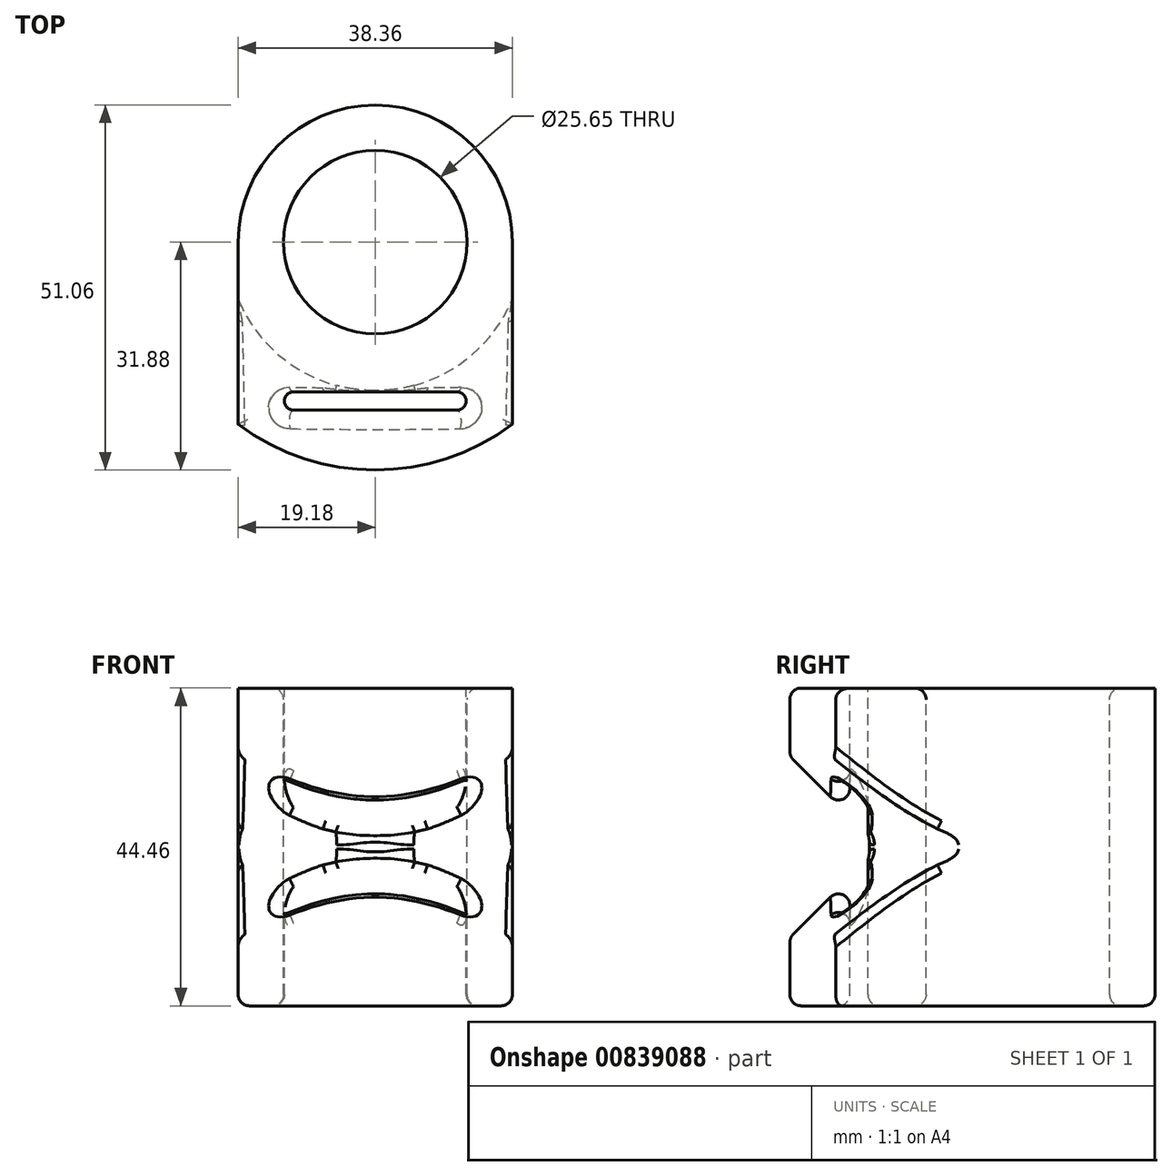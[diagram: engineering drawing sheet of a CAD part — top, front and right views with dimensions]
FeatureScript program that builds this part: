
annotation { "Feature Type Name" : "Feature", "Feature Type Description" : "" }
export const myFeature = defineFeature(function(context is Context, id is Id, definition is map)
    precondition{}
    {
        {
            var Q0;
            Q0=qCreatedBy(makeId("Front.planeOp"),FACE);
            var sketch = newSketch(context, id + "F0", { "sketchPlane" : qUnion([Q0])});
            skLineSegment(sketch, "E0", {"start": v(-12.83, -22.23) * mm, "end": v(-31.88, -22.23) * mm});
            skLineSegment(sketch, "E1", {"start": v(-31.88, -22.23) * mm, "end": v(-31.88, -12.7) * mm});
            skLineSegment(sketch, "E2", {"start": v(-31.88, -12.7) * mm, "end": v(-20.76, -1.59) * mm});
            skLineSegment(sketch, "E3", {"start": v(-20.76, -1.59) * mm, "end": v(-20.76, 0) * mm});
            skLineSegment(sketch, "E4", {"start": v(-12.83, -22.23) * mm, "end": v(-12.83, 0) * mm});
            skLineSegment(sketch, "E5", {"start": v(0, 0) * mm, "end": v(0, -22.22) * mm, "construction": true});
            skLineSegment(sketch, "E6", {"start": v(0, 0) * mm, "end": v(9.66, 0) * mm, "construction": true});
            skLineSegment(sketch, "E7.MirrorCS", {"start": v(-12.83, 22.23) * mm, "end": v(-12.83, 0) * mm});
            skLineSegment(sketch, "E8.MirrorCS", {"start": v(-12.83, 22.23) * mm, "end": v(-31.88, 22.23) * mm});
            skLineSegment(sketch, "E9.MirrorCS", {"start": v(-31.88, 22.23) * mm, "end": v(-31.88, 12.7) * mm});
            skLineSegment(sketch, "E10.MirrorCS", {"start": v(-31.88, 12.7) * mm, "end": v(-20.76, 1.59) * mm});
            skLineSegment(sketch, "E11.MirrorCS", {"start": v(-20.76, 1.59) * mm, "end": v(-20.76, 0) * mm});
            skSolve(sketch);
        }
        {
            var Q0;
            Q0=makeQuery(id+"F0.imprint","IMPRINT",FACE,{"disambiguationData":[TD([[makeQuery(id+"F0.imprint","IMPRINT",EDGE,{"derivedFrom":sQuery(id+"F0.wireOp",EDGE,"E0")}),-1.0]])]});
            var Q1;
            Q1=sQuery(id+"F0.wireOp",EDGE,"E5");
            revolve(context, id + "F1", {"surfaceOperationType" : NewSurfaceOperationType.NEW, "entities" : qUnion([Q0]), "axis" : qUnion([Q1]), "revolveType" : RevolveType.FULL});
        }
        {
            var Q0;
            Q0=makeQuery(id+"F1.opRevolve","SWEPT_FACE",FACE,{"disambiguationData":[OSD([sQuery(id+"F0.wireOp",EDGE,"E8.MirrorCS")])]});
            var sketch = newSketch(context, id + "F2", { "sketchPlane" : qUnion([Q0])});
            skLineSegment(sketch, "E12.bottom", {"start": v(-11.43, -23.5) * mm, "end": v(11.43, -23.5) * mm});
            skLineSegment(sketch, "E12.top", {"start": v(-11.43, -20.96) * mm, "end": v(11.43, -20.96) * mm});
            skLineSegment(sketch, "E12.left", {"start": v(-12.7, -22.23) * mm, "end": v(-12.7, -22.23) * mm});
            skLineSegment(sketch, "E12.right", {"start": v(12.7, -22.23) * mm, "end": v(12.7, -22.23) * mm});
            skPoint(sketch, "E12.middle", {"position": v(0, -22.23) * mm});
            skCircle(sketch, "E13", {"center": v(0, 0) * mm, "radius": 19.18 * mm});
            skLineSegment(sketch, "E14", {"start": v(0, 0) * mm, "end": v(0, -12.83) * mm, "construction": true});
            skLineSegment(sketch, "E15", {"start": v(-19.18, 0) * mm, "end": v(-19.18, -25.46) * mm});
            skLineSegment(sketch, "E16.MirrorCS", {"start": v(19.18, 0) * mm, "end": v(19.18, -25.46) * mm});
            skPoint(sketch, "E17.visualSharp", {"position": v(-12.7, -20.96) * mm});
            skArc(sketch, "E17.filletArc", {"start": v(-11.43, -20.96) * mm, "mid": v(-12.33, -21.33) * mm, "end": v(-12.7, -22.23) * mm});
            skPoint(sketch, "E18.visualSharp", {"position": v(-12.7, -23.5) * mm});
            skArc(sketch, "E18.filletArc", {"start": v(-12.7, -22.23) * mm, "mid": v(-12.33, -23.12) * mm, "end": v(-11.43, -23.5) * mm});
            skPoint(sketch, "E19.visualSharp", {"position": v(12.7, -20.96) * mm});
            skArc(sketch, "E19.filletArc", {"start": v(12.7, -22.23) * mm, "mid": v(12.33, -21.33) * mm, "end": v(11.43, -20.96) * mm});
            skPoint(sketch, "E20.visualSharp", {"position": v(12.7, -23.5) * mm});
            skArc(sketch, "E20.filletArc", {"start": v(11.43, -23.5) * mm, "mid": v(12.33, -23.12) * mm, "end": v(12.7, -22.23) * mm});
            skSolve(sketch);
        }
        {
            var Q0;
            Q0=makeQuery(id+"F2.imprint","IMPRINT",FACE,{"disambiguationData":[TD([[makeQuery(id+"F2.imprint","IMPRINT",EDGE,{"derivedFrom":sQuery(id+"F2.wireOp",EDGE,"E12.bottom")}),1.0]])]});
            extrude(context, id + "F3", {"entities" : qUnion([Q0]), "operationType" : NewBodyOperationType.REMOVE, "endBound" : BoundingType.THROUGH_ALL, "oppositeDirection" : true, "depth" : 25.4 * mm, "offsetDistance" : 25.4 * mm});
        }
        {
            var Q0;
            Q0=makeQuery(id+"F1.opRevolve","SWEPT_EDGE",EDGE,{"disambiguationData":[OSD([sQuery(id+"F0.wireOp",EDGE,"E2"),sQuery(id+"F0.wireOp",EDGE,"E3")])]});
            var Q1;
            Q1=makeQuery(id+"F1.opRevolve","SWEPT_EDGE",EDGE,{"disambiguationData":[OSD([sQuery(id+"F0.wireOp",EDGE,"E10.MirrorCS"),sQuery(id+"F0.wireOp",EDGE,"E11.MirrorCS")])]});
            fillet(context, id + "F4", {"entities" : qUnion([Q0, Q1]), "radius" : 3.17 * mm, "tangentPropagation" : true, "allowEdgeOverflow" : false});
        }
        {
            var Q0;
            {var subQ0=sQuery(id+"F2.wireOp",EDGE,"E15");Q0=makeQuery(id+"F2.imprint","IMPRINT",FACE,{"disambiguationData":[TD([[makeQuery(id+"F2.imprint","IMPRINT",EDGE,{"derivedFrom":subQ0}),-1.0]])]});}
            extrude(context, id + "F5", {"entities" : qUnion([Q0]), "operationType" : NewBodyOperationType.REMOVE, "endBound" : BoundingType.THROUGH_ALL, "oppositeDirection" : true, "depth" : 25.4 * mm, "offsetDistance" : 25.4 * mm});
        }
        {
            var Q0;
            Q0=makeQuery(id+"F1.opRevolve","SWEPT_FACE",FACE,{"disambiguationData":[OSD([sQuery(id+"F0.wireOp",EDGE,"E4"),sQuery(id+"F0.wireOp",EDGE,"E7.MirrorCS")])]});
            var Q1;
            Q1=makeQuery(id+"F5.boolean.opBoolean","COPY",EDGE,{"derivedFrom":makeQuery(id+"F5.opExtrude","CAP_EDGE",EDGE,{"disambiguationData":[OSD([sQuery(id+"F2.wireOp",EDGE,"E15")])],"isStart":true})});
            var Q2;
            Q2=makeQuery(id+"F1.opRevolve","SWEPT_EDGE",EDGE,{"disambiguationData":[OSD([sQuery(id+"F0.wireOp",EDGE,"E8.MirrorCS"),sQuery(id+"F0.wireOp",EDGE,"E9.MirrorCS")])]});
            var Q3;
            Q3=makeQuery(id+"F1.opRevolve","SWEPT_EDGE",EDGE,{"disambiguationData":[OSD([sQuery(id+"F0.wireOp",EDGE,"E0"),sQuery(id+"F0.wireOp",EDGE,"E1")])]});
            var Q4;
            Q4=makeQuery(id+"F5.boolean.opBoolean","INTERSECT",EDGE,{"derivedFrom":[makeQuery(id+"F1.opRevolve","SWEPT_FACE",FACE,{"disambiguationData":[OSD([sQuery(id+"F0.wireOp",EDGE,"E0")])]}),makeQuery(id+"F5.opExtrude","SWEPT_FACE",FACE,{"disambiguationData":[OSD([sQuery(id+"F2.wireOp",EDGE,"E15")])]})]});
            var Q5;
            Q5=makeQuery(id+"F1.opRevolve","SWEPT_EDGE",EDGE,{"disambiguationData":[OSD([sQuery(id+"F0.wireOp",EDGE,"E9.MirrorCS"),sQuery(id+"F0.wireOp",EDGE,"E10.MirrorCS")])]});
            var Q6;
            Q6=makeQuery(id+"F1.opRevolve","SWEPT_EDGE",EDGE,{"disambiguationData":[OSD([sQuery(id+"F0.wireOp",EDGE,"E1"),sQuery(id+"F0.wireOp",EDGE,"E2")])]});
            var Q7;
            Q7=makeQuery(id+"F5.boolean.opBoolean","INTERSECT",EDGE,{"derivedFrom":[makeQuery(id+"F1.opRevolve","SWEPT_FACE",FACE,{"disambiguationData":[OSD([sQuery(id+"F0.wireOp",EDGE,"E2")])]}),makeQuery(id+"F5.opExtrude","SWEPT_FACE",FACE,{"disambiguationData":[OSD([sQuery(id+"F2.wireOp",EDGE,"E15")])]})]});
            var Q8;
            Q8=makeQuery(id+"F5.boolean.opBoolean","INTERSECT",EDGE,{"derivedFrom":[makeQuery(id+"F1.opRevolve","SWEPT_FACE",FACE,{"disambiguationData":[OSD([sQuery(id+"F0.wireOp",EDGE,"E10.MirrorCS")])]}),makeQuery(id+"F5.opExtrude","SWEPT_FACE",FACE,{"disambiguationData":[OSD([sQuery(id+"F2.wireOp",EDGE,"E16.MirrorCS")])]})]});
            var Q9;
            Q9=makeQuery(id+"F5.boolean.opBoolean","INTERSECT",EDGE,{"derivedFrom":[makeQuery(id+"F1.opRevolve","SWEPT_FACE",FACE,{"disambiguationData":[OSD([sQuery(id+"F0.wireOp",EDGE,"E2")])]}),makeQuery(id+"F5.opExtrude","SWEPT_FACE",FACE,{"disambiguationData":[OSD([sQuery(id+"F2.wireOp",EDGE,"E16.MirrorCS")])]})]});
            var Q10;
            Q10=makeQuery(id+"F5.boolean.opBoolean","INTERSECT",EDGE,{"derivedFrom":[makeQuery(id+"F1.opRevolve","SWEPT_FACE",FACE,{"disambiguationData":[OSD([sQuery(id+"F0.wireOp",EDGE,"E10.MirrorCS")])]}),makeQuery(id+"F5.opExtrude","SWEPT_FACE",FACE,{"disambiguationData":[OSD([sQuery(id+"F2.wireOp",EDGE,"E15")])]})]});
            var Q11;
            {var subQ0=sQuery(id+"F2.wireOp",EDGE,"E15");Q11=makeQuery(id+"F5.boolean.opBoolean","COPY",EDGE,{"disambiguationData":[topologyDisambiguationEdgeConnected([makeQuery(id+"F1.opRevolve","SWEPT_FACE",FACE,{"disambiguationData":[OSD([sQuery(id+"F0.wireOp",EDGE,"E1")])]})])],"derivedFrom":makeQuery(id+"F5.opExtrude","SWEPT_EDGE",EDGE,{"disambiguationData":[OSD([sQuery(id+"F0.wireOp",EDGE,"E8.MirrorCS"),sQuery(id+"F0.wireOp",EDGE,"E9.MirrorCS"),subQ0])]})});}
            var Q12;
            {var subQ0=sQuery(id+"F2.wireOp",EDGE,"E16.MirrorCS");Q12=makeQuery(id+"F5.boolean.opBoolean","COPY",EDGE,{"disambiguationData":[topologyDisambiguationEdgeConnected([makeQuery(id+"F1.opRevolve","SWEPT_FACE",FACE,{"disambiguationData":[OSD([sQuery(id+"F0.wireOp",EDGE,"E1")])]})])],"derivedFrom":makeQuery(id+"F5.opExtrude","SWEPT_EDGE",EDGE,{"disambiguationData":[OSD([sQuery(id+"F0.wireOp",EDGE,"E8.MirrorCS"),sQuery(id+"F0.wireOp",EDGE,"E9.MirrorCS"),subQ0])]})});}
            var Q13;
            {var subQ0=sQuery(id+"F0.wireOp",EDGE,"E9.MirrorCS");var subQ1=sQuery(id+"F2.wireOp",EDGE,"E16.MirrorCS");Q13=makeQuery(id+"F5.boolean.opBoolean","COPY",EDGE,{"disambiguationData":[topologyDisambiguationEdgeConnected([makeQuery(id+"F1.opRevolve","SWEPT_FACE",FACE,{"disambiguationData":[OSD([subQ0])]})])],"derivedFrom":makeQuery(id+"F5.opExtrude","SWEPT_EDGE",EDGE,{"disambiguationData":[OSD([sQuery(id+"F0.wireOp",EDGE,"E8.MirrorCS"),subQ0,subQ1])]})});}
            var Q14;
            {var subQ0=sQuery(id+"F0.wireOp",EDGE,"E9.MirrorCS");var subQ1=sQuery(id+"F2.wireOp",EDGE,"E15");Q14=makeQuery(id+"F5.boolean.opBoolean","COPY",EDGE,{"disambiguationData":[topologyDisambiguationEdgeConnected([makeQuery(id+"F1.opRevolve","SWEPT_FACE",FACE,{"disambiguationData":[OSD([subQ0])]})])],"derivedFrom":makeQuery(id+"F5.opExtrude","SWEPT_EDGE",EDGE,{"disambiguationData":[OSD([sQuery(id+"F0.wireOp",EDGE,"E8.MirrorCS"),subQ0,subQ1])]})});}
            fillet(context, id + "F6", {"entities" : qUnion([Q0, Q1, Q2, Q3, Q4, Q5, Q6, Q7, Q8, Q9, Q10, Q11, Q12, Q13, Q14]), "radius" : 1.59 * mm, "tangentPropagation" : true, "allowEdgeOverflow" : false});
        }
        {
            var Q0;
            Q0=makeQuery(id+"F3.boolean.opBoolean","INTERSECT",EDGE,{"derivedFrom":[makeQuery(id+"F1.opRevolve","SWEPT_FACE",FACE,{"disambiguationData":[OSD([sQuery(id+"F0.wireOp",EDGE,"E0")])]}),makeQuery(id+"F3.opExtrude","SWEPT_FACE",FACE,{"disambiguationData":[OSD([sQuery(id+"F2.wireOp",EDGE,"E12.bottom")])]})]});
            var Q1;
            Q1=makeQuery(id+"F3.boolean.opBoolean","INTERSECT",EDGE,{"derivedFrom":[makeQuery(id+"F1.opRevolve","SWEPT_FACE",FACE,{"disambiguationData":[OSD([sQuery(id+"F0.wireOp",EDGE,"E2")])]}),makeQuery(id+"F3.opExtrude","SWEPT_FACE",FACE,{"disambiguationData":[OSD([sQuery(id+"F2.wireOp",EDGE,"E12.top")])]})]});
            var Q2;
            Q2=makeQuery(id+"F3.boolean.opBoolean","INTERSECT",EDGE,{"derivedFrom":[makeQuery(id+"F1.opRevolve","SWEPT_FACE",FACE,{"disambiguationData":[OSD([sQuery(id+"F0.wireOp",EDGE,"E10.MirrorCS")])]}),makeQuery(id+"F3.opExtrude","SWEPT_FACE",FACE,{"disambiguationData":[OSD([sQuery(id+"F2.wireOp",EDGE,"E12.top")])]})]});
            var Q3;
            Q3=makeQuery(id+"F3.boolean.opBoolean","COPY",EDGE,{"derivedFrom":makeQuery(id+"F3.opExtrude","CAP_EDGE",EDGE,{"disambiguationData":[OSD([sQuery(id+"F2.wireOp",EDGE,"E12.top")])],"isStart":true})});
            fillet(context, id + "F7", {"entities" : qUnion([Q0, Q1, Q2, Q3]), "radius" : 1.59 * mm, "tangentPropagation" : true, "allowEdgeOverflow" : false});
        }
    });
